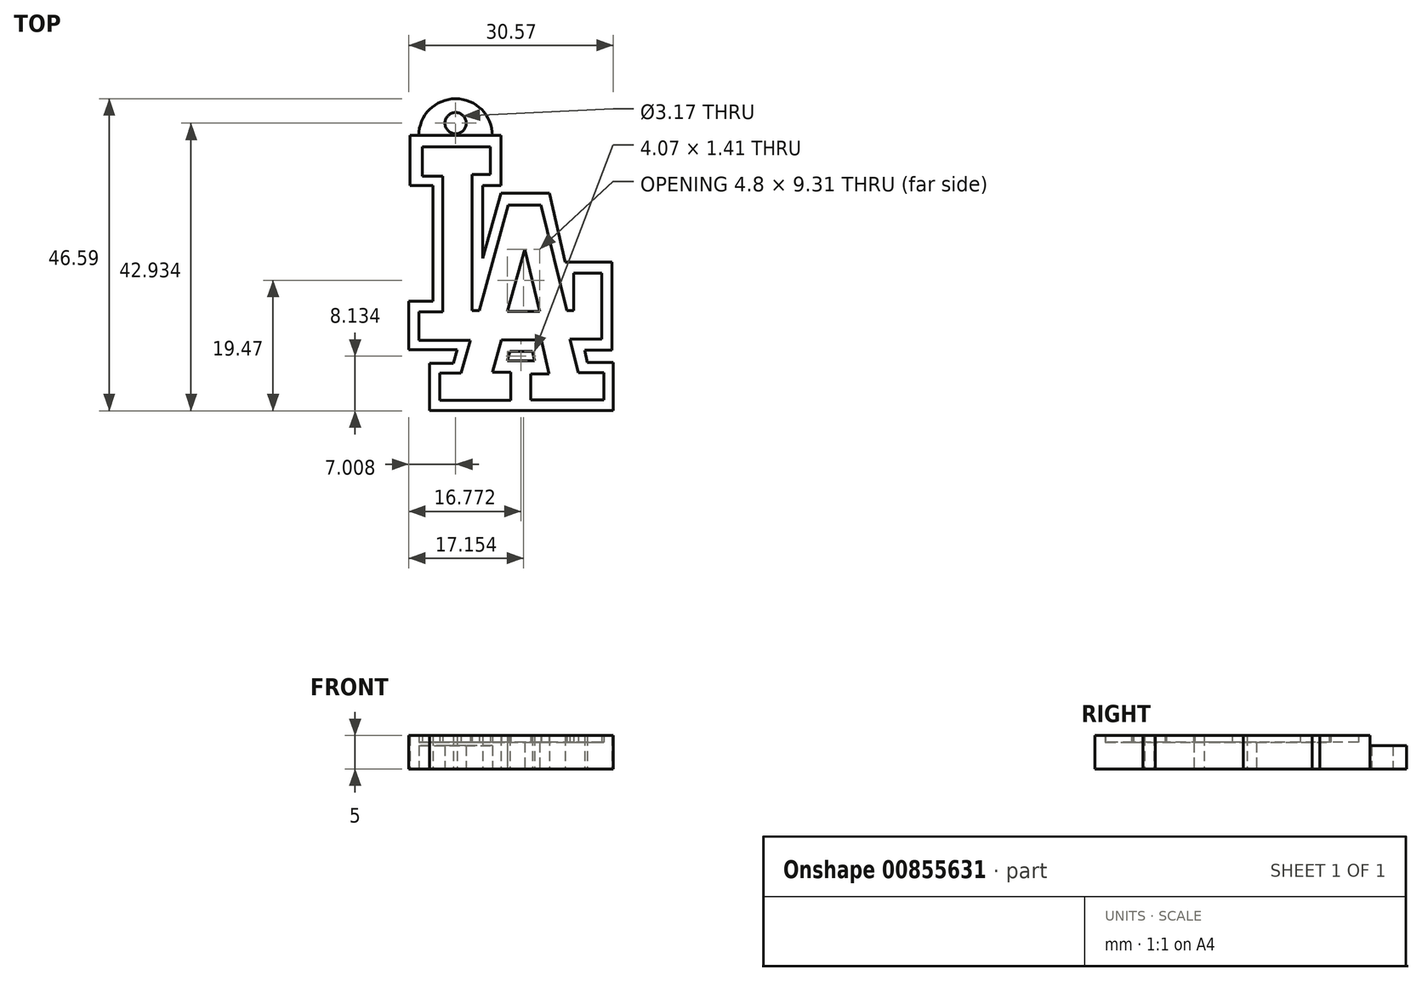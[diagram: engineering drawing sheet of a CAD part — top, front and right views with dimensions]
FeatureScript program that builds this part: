
annotation { "Feature Type Name" : "Feature", "Feature Type Description" : "" }
export const myFeature = defineFeature(function(context is Context, id is Id, definition is map)
    precondition{}
    {
        {
            var Q0;
            Q0=qCreatedBy(makeId("Top.planeOp"),FACE);
            var sketch = newSketch(context, id + "F0", { "sketchPlane" : qUnion([Q0])});
            skLineSegment(sketch, "E0", {"start": v(-16.07, 21.83) * mm, "end": v(-2.46, 21.83) * mm});
            skLineSegment(sketch, "E1", {"start": v(-2.46, 21.83) * mm, "end": v(-2.46, 14.35) * mm});
            skLineSegment(sketch, "E2", {"start": v(-2.46, 14.35) * mm, "end": v(-5.19, 14.35) * mm});
            skLineSegment(sketch, "E3", {"start": v(-5.19, 14.35) * mm, "end": v(-5.19, 3.53) * mm});
            skLineSegment(sketch, "E4", {"start": v(-5.19, 3.53) * mm, "end": v(-2.5, 13.22) * mm});
            skLineSegment(sketch, "E5", {"start": v(-2.5, 13.22) * mm, "end": v(4.76, 13.22) * mm});
            skLineSegment(sketch, "E6", {"start": v(4.76, 13.22) * mm, "end": v(7.13, 2.9) * mm});
            skLineSegment(sketch, "E7", {"start": v(7.13, 2.9) * mm, "end": v(14.1, 2.9) * mm});
            skLineSegment(sketch, "E8", {"start": v(14.1, 2.9) * mm, "end": v(14.1, -10.24) * mm});
            skLineSegment(sketch, "E9", {"start": v(14.1, -10.24) * mm, "end": v(10.02, -10.24) * mm});
            skLineSegment(sketch, "E10", {"start": v(10.02, -10.24) * mm, "end": v(10.38, -12.04) * mm});
            skLineSegment(sketch, "E11", {"start": v(10.38, -12.04) * mm, "end": v(14.3, -12.04) * mm});
            skLineSegment(sketch, "E12", {"start": v(14.3, -12.04) * mm, "end": v(14.3, -19.26) * mm});
            skLineSegment(sketch, "E13", {"start": v(14.3, -19.26) * mm, "end": v(-13.13, -19.26) * mm});
            skLineSegment(sketch, "E14", {"start": v(-13.13, -19.26) * mm, "end": v(-13.13, -12.2) * mm});
            skLineSegment(sketch, "E15", {"start": v(-13.13, -12.2) * mm, "end": v(-9.57, -12.2) * mm});
            skLineSegment(sketch, "E16", {"start": v(-9.57, -12.2) * mm, "end": v(-9, -10.13) * mm});
            skLineSegment(sketch, "E17", {"start": v(-9, -10.13) * mm, "end": v(-16.27, -10.13) * mm});
            skLineSegment(sketch, "E18", {"start": v(-16.27, -10.13) * mm, "end": v(-16.27, -2.92) * mm});
            skLineSegment(sketch, "E19", {"start": v(-16.27, -2.92) * mm, "end": v(-12.66, -2.92) * mm});
            skLineSegment(sketch, "E20", {"start": v(-12.66, -2.92) * mm, "end": v(-12.66, 14.35) * mm});
            skLineSegment(sketch, "E21", {"start": v(-16.07, 21.83) * mm, "end": v(-16.07, 14.35) * mm});
            skLineSegment(sketch, "E22", {"start": v(-12.66, 14.35) * mm, "end": v(-16.07, 14.35) * mm});
            skLineSegment(sketch, "E23", {"start": v(-14.24, 20.11) * mm, "end": v(-4.1, 20.11) * mm});
            skLineSegment(sketch, "E24", {"start": v(-4.1, 20.11) * mm, "end": v(-4.1, 16.04) * mm});
            skLineSegment(sketch, "E25", {"start": v(-4.1, 16.04) * mm, "end": v(-6.83, 16.04) * mm});
            skLineSegment(sketch, "E26", {"start": v(-6.83, 16.04) * mm, "end": v(-6.83, -4.3) * mm});
            skLineSegment(sketch, "E27", {"start": v(-6.83, -4.3) * mm, "end": v(-5.7, -4.3) * mm});
            skLineSegment(sketch, "E28", {"start": v(-5.7, -4.3) * mm, "end": v(-1.4, 11.44) * mm});
            skLineSegment(sketch, "E29", {"start": v(-1.4, 11.44) * mm, "end": v(3.49, 11.44) * mm});
            skLineSegment(sketch, "E30", {"start": v(3.49, 11.44) * mm, "end": v(7.35, -4.34) * mm});
            skLineSegment(sketch, "E31", {"start": v(7.35, -4.34) * mm, "end": v(8.39, -4.34) * mm});
            skLineSegment(sketch, "E32", {"start": v(8.39, -4.34) * mm, "end": v(8.39, 1.26) * mm});
            skLineSegment(sketch, "E33", {"start": v(8.39, 1.26) * mm, "end": v(12.55, 1.26) * mm});
            skLineSegment(sketch, "E34", {"start": v(12.55, 1.26) * mm, "end": v(12.55, -8.54) * mm});
            skLineSegment(sketch, "E35", {"start": v(12.55, -8.54) * mm, "end": v(7.82, -8.54) * mm});
            skLineSegment(sketch, "E36", {"start": v(7.82, -8.54) * mm, "end": v(9.08, -13.57) * mm});
            skLineSegment(sketch, "E37", {"start": v(9.08, -13.57) * mm, "end": v(12.9, -13.57) * mm});
            skLineSegment(sketch, "E38", {"start": v(12.9, -13.57) * mm, "end": v(12.9, -17.65) * mm});
            skLineSegment(sketch, "E39", {"start": v(12.9, -17.65) * mm, "end": v(1.93, -17.65) * mm});
            skLineSegment(sketch, "E40", {"start": v(1.93, -17.65) * mm, "end": v(1.93, -13.74) * mm});
            skLineSegment(sketch, "E41", {"start": v(1.93, -13.74) * mm, "end": v(4.7, -13.74) * mm});
            skLineSegment(sketch, "E42", {"start": v(4.7, -13.74) * mm, "end": v(3.58, -8.67) * mm});
            skLineSegment(sketch, "E43", {"start": v(3.58, -8.67) * mm, "end": v(-2.4, -8.67) * mm});
            skLineSegment(sketch, "E44", {"start": v(-2.4, -8.67) * mm, "end": v(-3.75, -13.48) * mm});
            skLineSegment(sketch, "E45", {"start": v(-3.75, -13.48) * mm, "end": v(-1.02, -13.48) * mm});
            skLineSegment(sketch, "E46", {"start": v(-1.02, -13.48) * mm, "end": v(-1.02, -17.69) * mm});
            skLineSegment(sketch, "E47", {"start": v(-1.02, -17.69) * mm, "end": v(-11.64, -17.69) * mm});
            skLineSegment(sketch, "E48", {"start": v(-11.64, -17.69) * mm, "end": v(-11.64, -13.61) * mm});
            skLineSegment(sketch, "E49", {"start": v(-11.64, -13.61) * mm, "end": v(-8.48, -13.61) * mm});
            skLineSegment(sketch, "E50", {"start": v(-8.48, -13.61) * mm, "end": v(-7.05, -8.76) * mm});
            skLineSegment(sketch, "E51", {"start": v(-7.05, -8.76) * mm, "end": v(-14.72, -8.76) * mm});
            skLineSegment(sketch, "E52", {"start": v(-14.72, -8.76) * mm, "end": v(-14.72, -4.51) * mm});
            skLineSegment(sketch, "E53", {"start": v(-14.72, -4.51) * mm, "end": v(-11.16, -4.51) * mm});
            skLineSegment(sketch, "E54", {"start": v(-11.16, -4.51) * mm, "end": v(-11.16, 15.78) * mm});
            skLineSegment(sketch, "E55", {"start": v(-11.16, 15.78) * mm, "end": v(-14.24, 15.78) * mm});
            skLineSegment(sketch, "E56", {"start": v(-14.24, 20.11) * mm, "end": v(-14.24, 15.78) * mm});
            skLineSegment(sketch, "E57", {"start": v(1.06, 4.86) * mm, "end": v(-1.52, -4.44) * mm});
            skLineSegment(sketch, "E58", {"start": v(-1.52, -4.44) * mm, "end": v(3.28, -4.44) * mm});
            skLineSegment(sketch, "E59", {"start": v(3.28, -4.44) * mm, "end": v(1.06, 4.86) * mm});
            skLineSegment(sketch, "E60", {"start": v(-1.15, -10.42) * mm, "end": v(-1.54, -11.83) * mm});
            skLineSegment(sketch, "E61", {"start": v(-1.54, -11.83) * mm, "end": v(2.54, -11.83) * mm});
            skLineSegment(sketch, "E62", {"start": v(-1.15, -10.42) * mm, "end": v(2.21, -10.42) * mm});
            skLineSegment(sketch, "E63", {"start": v(2.21, -10.42) * mm, "end": v(2.54, -11.83) * mm});
            skArc(sketch, "E64", {"start": v(-3.76, 21.83) * mm, "mid": v(-9.26, 27.33) * mm, "end": v(-14.76, 21.83) * mm});
            skCircle(sketch, "E65", {"center": v(-9.26, 23.67) * mm, "radius": 1.59 * mm});
            skSolve(sketch);
        }
        {
            var Q0;
            {var subQ5=sQuery(id+"F0.wireOp",EDGE,"E1");Q0=makeQuery(id+"F0.imprint","IMPRINT",FACE,{"disambiguationData":[TD([[makeQuery(id+"F0.imprint","IMPRINT",EDGE,{"derivedFrom":subQ5}),-1.0]])]});}
            extrude(context, id + "F1", {"entities" : qUnion([Q0]), "depth" : 5 * mm, "offsetDistance" : 25 * mm});
        }
        {
            var Q0;
            {var subQ0=sQuery(id+"F0.wireOp",EDGE,"E64");Q0=makeQuery(id+"F0.imprint","IMPRINT",FACE,{"disambiguationData":[TD([[makeQuery(id+"F0.imprint","IMPRINT",EDGE,{"derivedFrom":subQ0}),1.0]])]});}
            extrude(context, id + "F2", {"entities" : qUnion([Q0]), "operationType" : NewBodyOperationType.ADD, "depth" : 3.5 * mm, "offsetDistance" : 25 * mm});
        }
        {
            var Q0;
            Q0=makeQuery(id+"F0.imprint","IMPRINT",FACE,{"disambiguationData":[TD([[makeQuery(id+"F0.imprint","IMPRINT",EDGE,{"derivedFrom":sQuery(id+"F0.wireOp",EDGE,"E23")}),-1.0]])]});
            extrude(context, id + "F3", {"entities" : qUnion([Q0]), "operationType" : NewBodyOperationType.ADD, "depth" : 4 * mm, "offsetDistance" : 25 * mm});
        }
    });
